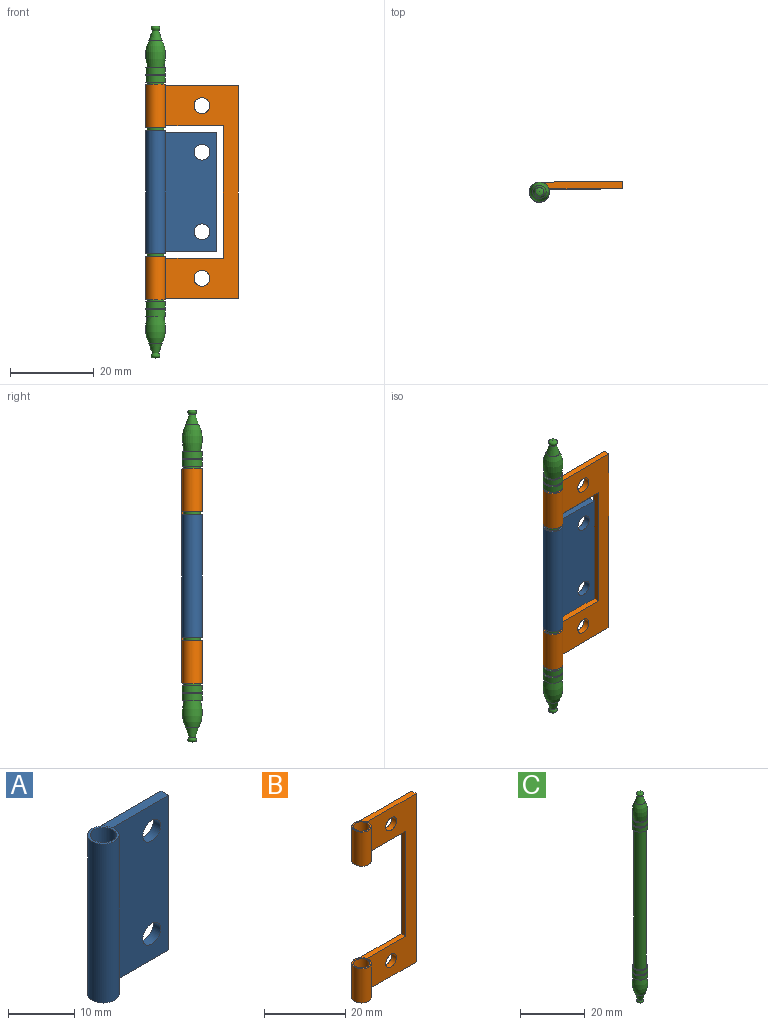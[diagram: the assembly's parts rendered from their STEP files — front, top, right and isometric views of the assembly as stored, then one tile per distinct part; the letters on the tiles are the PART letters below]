
ASSEMBLY  parts=3 mates=2
PART A: 11 faces, bbox 17.1x4.8x29.4 mm
  f0: plane 14.68x1.59mm, normal (0,0,1), area 20.7mm2, adj f2,f3,f4,f8
  f1: plane 14.68x1.59mm, normal (0,0,-1), area 20.7mm2, adj f2,f3,f4,f8
  f2: plane 28.58x1.59mm, normal (1,0,0), area 45.4mm2, adj f0,f1,f3,f4
  f3: plane 28.58x12.44mm, normal (0,-1,0), area 332.8mm2, adj f0,f1,f2,f5,f6,f8
  f4: plane 28.58x14.68mm, normal (0,1,0), area 397mm2, adj f0,f1,f2,f5,f6,f8
  f5: cylinder r=1.9mm len=3.8mm, axis (0,1,0), area 18.9mm2, adj f3,f4
  f6: cylinder r=1.9mm len=3.8mm, axis (0,1,0), area 18.9mm2, adj f3,f4
  f7: plane 4.76x4.76mm, normal (0,0,-1), area 5.4mm2, adj f8,f10
  f8: cylinder r=2.38mm len=29.37mm, axis (0,0,1), area 355.7mm2, adj f0,f1,f3,f4,f7,f9
  f9: plane 4.76x4.76mm, normal (0,0,1), area 5.4mm2, adj f8,f10
  f10: cylinder r=1.98mm len=29.37mm, axis (0,0,1), area 366.2mm2, adj f7,f9
PART B: 18 faces, bbox 22.2x4.8x51.6 mm
  f0: plane 31.75x1.59mm, normal (-1,0,0), area 50.4mm2, adj f5,f7,f8,f12
  f1: plane 50.8x1.59mm, normal (1,0,0), area 80.6mm2, adj f4,f6,f7,f12
  f2: cylinder r=1.9mm len=3.8mm, axis (0,1,0), area 18.9mm2, adj f7,f12
  f3: cylinder r=1.9mm len=3.8mm, axis (0,1,0), area 18.9mm2, adj f7,f12
  f4: plane 19.84x1.59mm, normal (0,0,-1), area 28.9mm2, adj f1,f7,f10,f12
  f5: plane 16.27x1.59mm, normal (0,0,1), area 23.2mm2, adj f0,f7,f10,f12
  f6: plane 19.84x1.59mm, normal (0,0,1), area 28.9mm2, adj f1,f7,f12,f14
  f7: plane 50.8x17.6mm, normal (0,-1,0), area 426mm2, adj f0,f1,f2,f3,f4,f5,f6,f8
  f8: plane 16.27x1.59mm, normal (0,0,-1), area 23.2mm2, adj f0,f7,f12,f14
  f9: plane 4.76x4.76mm, normal (0,0,-1), area 5.4mm2, adj f10,f17
  f10: cylinder r=2.38mm len=10.32mm, axis (0,0,1), area 126.5mm2, adj f4,f5,f7,f9,f11,f12
  f11: plane 4.76x4.76mm, normal (0,0,1), area 5.4mm2, adj f10,f17
  f12: plane 50.8x19.84mm, normal (0,1,0), area 468.8mm2, adj f0,f1,f2,f3,f4,f5,f6,f8
  f13: plane 4.76x4.76mm, normal (0,0,-1), area 5.4mm2, adj f14,f16
  f14: cylinder r=2.38mm len=10.32mm, axis (0,0,1), area 126.5mm2, adj f6,f7,f8,f12,f13,f15
  f15: plane 4.76x4.76mm, normal (0,0,1), area 5.4mm2, adj f14,f16
  f16: cylinder r=1.98mm len=10.32mm, axis (0,0,1), area 128.7mm2, adj f13,f15
  f17: cylinder r=1.98mm len=10.32mm, axis (0,0,1), area 128.7mm2, adj f9,f11
PART C: 21 faces, bbox 4.8x4.8x79.4 mm
  f0: plane 4.76x4.76mm, normal (0,0,-1), area 5.4mm2, adj f1,f6
  f1: cylinder r=2.38mm len=4.76mm, axis (0,0,1), area 23.8mm2, adj f0,f2
  f2: plane 4.76x4.76mm, normal (0,0,1), area 5.4mm2, adj f1,f5
  f3: revolved ~2.12x2.12mm, area 9.5mm2, adj f4
  f4: cone r=0.79mm half-angle=18.4deg, axis (0,0,-1), area 18.8mm2, adj f3,f5
  f5: revolved ~6.35x4.76mm, area 89.3mm2, adj f2,f4
  f6: cylinder r=1.98mm len=3.97mm, axis (0,0,1), area 4.9mm2, adj f0,f9
  f7: plane 4.76x4.76mm, normal (0,0,-1), area 5.4mm2, adj f8,f10
  f8: cylinder r=2.38mm len=4.76mm, axis (0,0,1), area 23.8mm2, adj f7,f9
  f9: plane 4.76x4.76mm, normal (0,0,1), area 5.4mm2, adj f6,f8
  f10: cylinder r=1.98mm len=52.39mm, axis (0,0,1), area 653.2mm2, adj f7,f13
  f11: plane 4.76x4.76mm, normal (0,0,-1), area 5.4mm2, adj f12,f14
  f12: cylinder r=2.38mm len=4.76mm, axis (0,0,1), area 23.8mm2, adj f11,f13
  f13: plane 4.76x4.76mm, normal (0,0,1), area 5.4mm2, adj f10,f12
  f14: cylinder r=1.98mm len=3.97mm, axis (0,0,1), area 4.9mm2, adj f11,f17
  f15: plane 4.76x4.76mm, normal (0,0,-1), area 5.4mm2, adj f16,f20
  f16: cylinder r=2.38mm len=4.76mm, axis (0,0,1), area 23.8mm2, adj f15,f17
  f17: plane 4.76x4.76mm, normal (0,0,1), area 5.4mm2, adj f14,f16
  f18: cone r=0.79mm half-angle=18.4deg, axis (0,0,1), area 18.8mm2, adj f19,f20
  f19: revolved ~2.12x2.12mm, area 9.5mm2, adj f18
  f20: revolved ~6.35x4.76mm, area 89.3mm2, adj f15,f18
PLACE A rot(axis=(0,0,-1),0.2deg) t=(190.87,55.8,-519.61)mm
PLACE B rot(axis=(0,0,1),0.3deg) t=(190.37,57.47,-519.61)mm
PLACE C t=(190.7,56.36,-519.61)mm fixed
MATE revolute B.f10 <-> C.f1  axis (0,0,1) through (0,0,0)mm
MATE revolute C.f1 <-> A.f8  axis (0,0,1) through (0,0,0)mm
